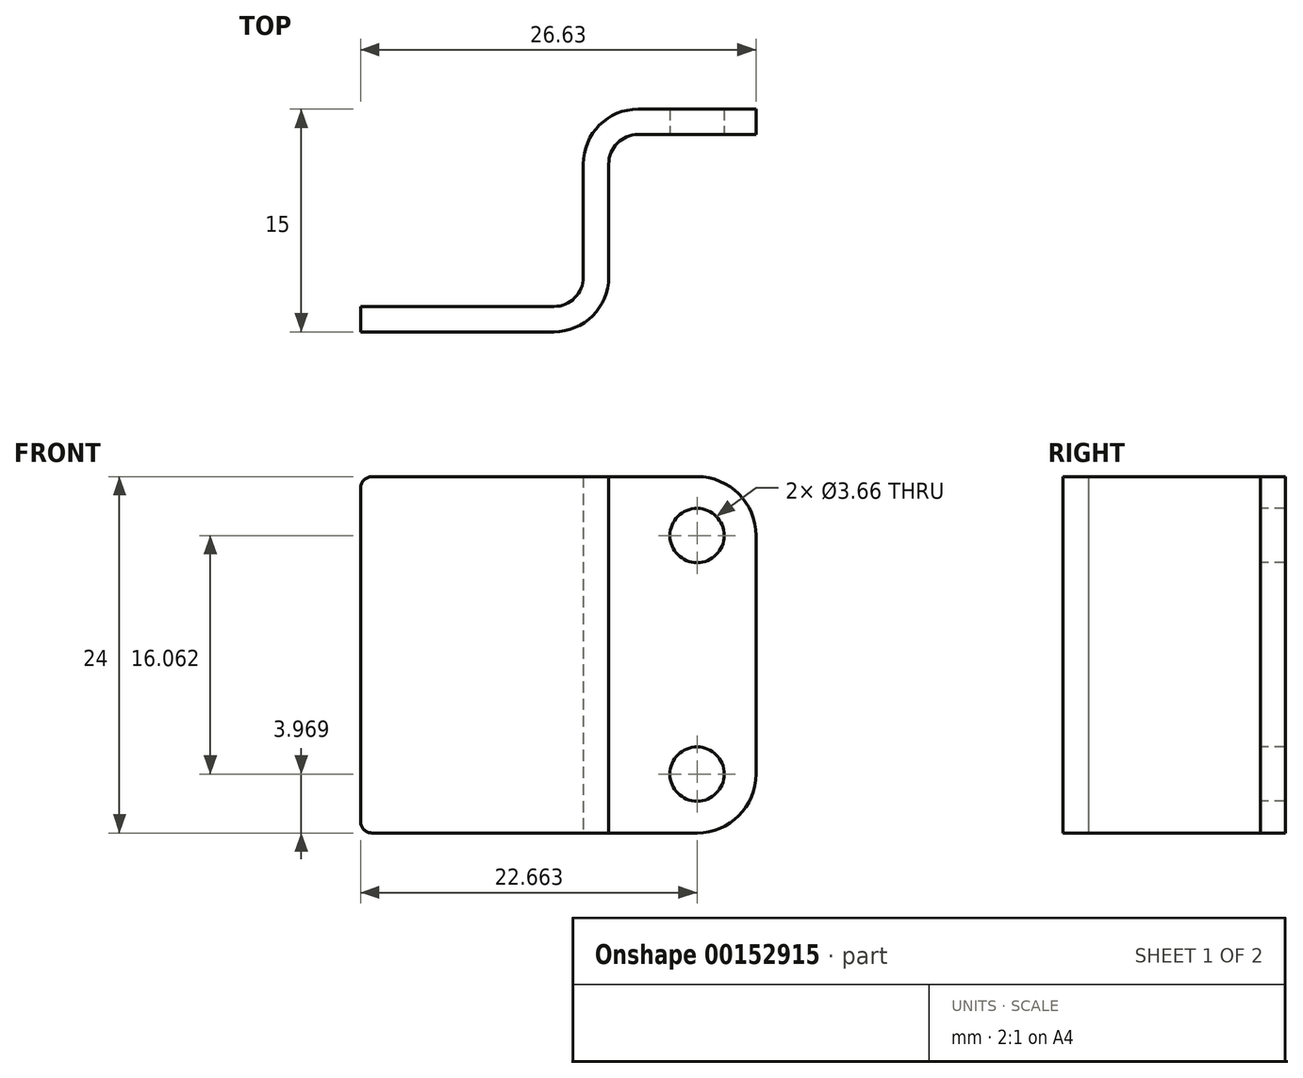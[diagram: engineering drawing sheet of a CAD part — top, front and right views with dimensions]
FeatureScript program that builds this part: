
annotation { "Feature Type Name" : "Feature", "Feature Type Description" : "" }
export const myFeature = defineFeature(function(context is Context, id is Id, definition is map)
    precondition{}
    {
        {
            var Q0;
            Q0=qCreatedBy(makeId("Top.planeOp"),FACE);
            var sketch = newSketch(context, id + "F0", { "sketchPlane" : qUnion([Q0])});
            skLineSegment(sketch, "E0.left", {"start": v(0, 0) * mm, "end": v(0, -13.3) * mm});
            skLineSegment(sketch, "E0.right", {"start": v(-1.7, 1.7) * mm, "end": v(-1.7, -11.58) * mm});
            skLineSegment(sketch, "E1.bottom", {"start": v(-1.7, -11.58) * mm, "end": v(-16.7, -11.58) * mm});
            skLineSegment(sketch, "E1.top", {"start": v(0, -13.3) * mm, "end": v(-16.7, -13.3) * mm});
            skLineSegment(sketch, "E1.right", {"start": v(-16.7, -11.58) * mm, "end": v(-16.7, -13.3) * mm});
            skLineSegment(sketch, "E2.bottom", {"start": v(0, 0) * mm, "end": v(9.92, 0) * mm});
            skLineSegment(sketch, "E2.top", {"start": v(-1.7, 1.7) * mm, "end": v(9.92, 1.7) * mm});
            skLineSegment(sketch, "E2.right", {"start": v(9.92, 0) * mm, "end": v(9.92, 1.7) * mm});
            skLineSegment(sketch, "E3", {"start": v(0, -6.65) * mm, "end": v(-1.7, -6.65) * mm, "construction": true});
            skSolve(sketch);
        }
        {
            var Q0;
            Q0=qSketchRegion(id+"F0",true);
            extrude(context, id + "F1", {"entities" : qUnion([Q0]), "depth" : 24 * mm});
        }
        {
            var Q0;
            Q0=makeQuery(id+"F1.opExtrude","SWEPT_EDGE",EDGE,{"disambiguationData":[OSD([sQuery(id+"F0.wireOp",EDGE,"E0.left"),sQuery(id+"F0.wireOp",EDGE,"E2.bottom")])]});
            var Q1;
            Q1=makeQuery(id+"F1.opExtrude","SWEPT_EDGE",EDGE,{"disambiguationData":[OSD([sQuery(id+"F0.wireOp",EDGE,"E0.right"),sQuery(id+"F0.wireOp",EDGE,"E1.bottom")])]});
            fillet(context, id + "F2", {"entities" : qUnion([Q0, Q1]), "radius" : 1.98 * mm, "tangentPropagation" : true, "allowEdgeOverflow" : false});
        }
        {
            var Q0;
            Q0=makeQuery(id+"F1.opExtrude","SWEPT_EDGE",EDGE,{"disambiguationData":[OSD([sQuery(id+"F0.wireOp",EDGE,"E0.left"),sQuery(id+"F0.wireOp",EDGE,"E1.top")])]});
            var Q1;
            Q1=makeQuery(id+"F1.opExtrude","SWEPT_EDGE",EDGE,{"disambiguationData":[OSD([sQuery(id+"F0.wireOp",EDGE,"E0.right"),sQuery(id+"F0.wireOp",EDGE,"E2.top")])]});
            fillet(context, id + "F3", {"entities" : qUnion([Q0, Q1]), "radius" : 3.7 * mm, "tangentPropagation" : true, "allowEdgeOverflow" : false});
        }
        {
            var Q0;
            Q0=makeQuery(id+"F1.opExtrude","CAP_EDGE",EDGE,{"disambiguationData":[OSD([sQuery(id+"F0.wireOp",EDGE,"E2.right")])],"isStart":false});
            var Q1;
            Q1=makeQuery(id+"F1.opExtrude","CAP_EDGE",EDGE,{"disambiguationData":[OSD([sQuery(id+"F0.wireOp",EDGE,"E2.right")])],"isStart":true});
            fillet(context, id + "F4", {"entities" : qUnion([Q0, Q1]), "radius" : 3.97 * mm, "tangentPropagation" : true, "allowEdgeOverflow" : false});
        }
        {
            var Q0;
            Q0=makeQuery(id+"F1.opExtrude","CAP_EDGE",EDGE,{"disambiguationData":[OSD([sQuery(id+"F0.wireOp",EDGE,"E1.right")])],"isStart":true});
            var Q1;
            Q1=makeQuery(id+"F1.opExtrude","CAP_EDGE",EDGE,{"disambiguationData":[OSD([sQuery(id+"F0.wireOp",EDGE,"E1.right")])],"isStart":false});
            fillet(context, id + "F5", {"entities" : qUnion([Q0, Q1]), "radius" : 0.76 * mm, "tangentPropagation" : true, "allowEdgeOverflow" : false});
        }
        {
            var Q0;
            Q0=makeQuery(id+"F1.opExtrude","SWEPT_FACE",FACE,{"disambiguationData":[OSD([sQuery(id+"F0.wireOp",EDGE,"E2.bottom")])]});
            var sketch = newSketch(context, id + "F6", { "sketchPlane" : qUnion([Q0])});
            skCircle(sketch, "E4", {"center": v(5.95, 20.03) * mm, "radius": 1.83 * mm});
            skCircle(sketch, "E5", {"center": v(5.95, 3.97) * mm, "radius": 1.83 * mm});
            skSolve(sketch);
        }
        {
            var Q0;
            Q0=qSketchRegion(id+"F6",true);
            var Q1;
            Q1=makeQuery(id+"F1.opExtrude","SWEPT_FACE",FACE,{"disambiguationData":[OSD([sQuery(id+"F0.wireOp",EDGE,"E2.top")])]});
            extrude(context, id + "F7", {"entities" : qUnion([Q0]), "operationType" : NewBodyOperationType.REMOVE, "endBound" : BoundingType.UP_TO_SURFACE, "oppositeDirection" : true, "endBoundEntityFace" : qUnion([Q1]), "depth" : 25.4 * mm});
        }
    });
